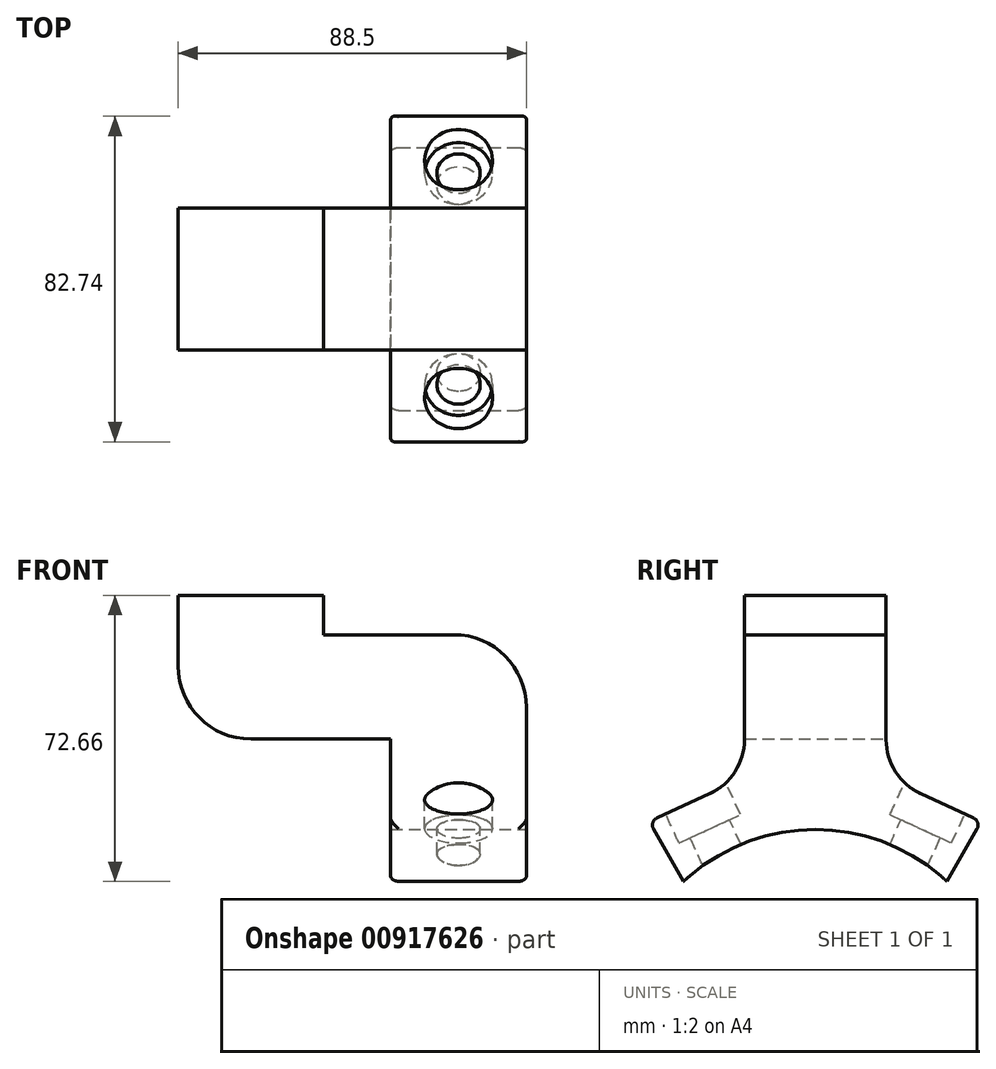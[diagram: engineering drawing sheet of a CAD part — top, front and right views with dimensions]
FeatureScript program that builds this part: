
annotation { "Feature Type Name" : "Feature", "Feature Type Description" : "" }
export const myFeature = defineFeature(function(context is Context, id is Id, definition is map)
    precondition{}
    {
        {
            var Q0;
            Q0=qCreatedBy(makeId("Front.planeOp"),FACE);
            var sketch = newSketch(context, id + "F0", { "sketchPlane" : qUnion([Q0])});
            skLineSegment(sketch, "E0", {"start": v(0, 0) * mm, "end": v(-88.5, 0) * mm});
            skLineSegment(sketch, "E1", {"start": v(-88.5, 0) * mm, "end": v(-88.5, 36.5) * mm});
            skLineSegment(sketch, "E2", {"start": v(-88.5, 36.5) * mm, "end": v(-51.5, 36.5) * mm});
            skLineSegment(sketch, "E3", {"start": v(-51.5, 36.5) * mm, "end": v(-51.5, 26.5) * mm});
            skLineSegment(sketch, "E4", {"start": v(-51.5, 26.5) * mm, "end": v(0, 26.5) * mm});
            skLineSegment(sketch, "E5", {"start": v(0, 26.5) * mm, "end": v(0, 0) * mm});
            skSolve(sketch);
        }
        {
            var Q0;
            Q0 = qSketchRegion(id + "F0", true);
            extrude(context, id + "F1", {"entities" : qUnion([Q0]), "endBound" : BoundingType.SYMMETRIC, "depth" : 36 * mm, "offsetDistance" : 25 * mm});
        }
        {
            var Q0;
            Q0=makeQuery(id+"F1.opExtrude","SWEPT_EDGE",EDGE,{"disambiguationData":[OSD([sQuery(id+"F0.wireOp",EDGE,"E4"),sQuery(id+"F0.wireOp",EDGE,"E5")])]});
            var Q1;
            Q1=makeQuery(id+"F1.opExtrude","SWEPT_EDGE",EDGE,{"disambiguationData":[OSD([sQuery(id+"F0.wireOp",EDGE,"E0"),sQuery(id+"F0.wireOp",EDGE,"E1")])]});
            fillet(context, id + "F2", {"entities" : qUnion([Q0, Q1]), "radius" : 18.5 * mm, "tangentPropagation" : true, "allowEdgeOverflow" : false});
        }
        {
            var Q0;
            Q0=makeQuery(id+"F1.opExtrude","SWEPT_FACE",FACE,{"disambiguationData":[OSD([sQuery(id+"F0.wireOp",EDGE,"E5")])]});
            var sketch = newSketch(context, id + "F3", { "sketchPlane" : qUnion([Q0])});
            skArc(sketch, "E6", {"start": v(-33.42, -36.16) * mm, "mid": v(0, -23) * mm, "end": v(33.42, -36.16) * mm});
            skArc(sketch, "E7", {"start": v(-41.07, -22.91) * mm, "mid": v(0, -8) * mm, "end": v(41.07, -22.91) * mm});
            skLineSegment(sketch, "E8", {"start": v(-41.07, -22.91) * mm, "end": v(-33.42, -36.16) * mm});
            skLineSegment(sketch, "E9", {"start": v(33.42, -36.16) * mm, "end": v(41.07, -22.91) * mm});
            skLineSegment(sketch, "E10", {"start": v(-33.42, -36.16) * mm, "end": v(0, -72) * mm, "construction": true});
            skLineSegment(sketch, "E11", {"start": v(0, -72) * mm, "end": v(33.42, -36.16) * mm, "construction": true});
            skLineSegment(sketch, "E12", {"start": v(-18, -10.58) * mm, "end": v(-18, 0) * mm});
            skLineSegment(sketch, "E13", {"start": v(-18, 0) * mm, "end": v(18, 0) * mm});
            skLineSegment(sketch, "E14", {"start": v(18, 0) * mm, "end": v(18, -10.58) * mm});
            skSolve(sketch);
        }
        {
            var Q0;
            Q0 = qSketchRegion(id + "F3", true);
            extrude(context, id + "F4", {"entities" : qUnion([Q0]), "operationType" : NewBodyOperationType.ADD, "oppositeDirection" : true, "depth" : 34.5 * mm, "offsetDistance" : 25 * mm});
        }
        {
            var Q0;
            Q0=makeQuery(id+"F4.opExtrude","SWEPT_EDGE",EDGE,{"disambiguationData":[OSD([sQuery(id+"F3.wireOp",EDGE,"E7"),sQuery(id+"F3.wireOp",EDGE,"E12")])]});
            var Q1;
            Q1=makeQuery(id+"F4.opExtrude","SWEPT_EDGE",EDGE,{"disambiguationData":[OSD([sQuery(id+"F3.wireOp",EDGE,"E7"),sQuery(id+"F3.wireOp",EDGE,"E14")])]});
            fillet(context, id + "F5", {"entities" : qUnion([Q0, Q1]), "radius" : 15 * mm, "tangentPropagation" : true, "allowEdgeOverflow" : false});
        }
        {
            var Q0;
            Q0=makeQuery(id+"F4.boolean.opBoolean","MERGE",FACE,{"derivedFrom":[makeQuery(id+"F1.opExtrude","SWEPT_FACE",FACE,{"disambiguationData":[OSD([sQuery(id+"F0.wireOp",EDGE,"E5")])]}),makeQuery(id+"F4.opExtrude","CAP_FACE",FACE,{"disambiguationData":[OSD([sQuery(id+"F3.wireOp",EDGE,"E6"),sQuery(id+"F3.wireOp",EDGE,"E7"),sQuery(id+"F3.wireOp",EDGE,"E8"),sQuery(id+"F3.wireOp",EDGE,"E9"),sQuery(id+"F3.wireOp",EDGE,"E12"),sQuery(id+"F3.wireOp",EDGE,"E13"),sQuery(id+"F3.wireOp",EDGE,"E14")])],"isStart":true})]});
            var sketch = newSketch(context, id + "F6", { "sketchPlane" : qUnion([Q0])});
            skLineSegment(sketch, "E15", {"start": v(-26.73, -13.85) * mm, "end": v(-42.2, -20.96) * mm});
            skLineSegment(sketch, "E16", {"start": v(-42.2, -20.96) * mm, "end": v(-41.07, -22.91) * mm});
            skLineSegment(sketch, "E17", {"start": v(-41.07, -22.91) * mm, "end": v(-26.73, -13.85) * mm});
            skLineSegment(sketch, "E18", {"start": v(26.73, -13.85) * mm, "end": v(42.2, -20.96) * mm});
            skLineSegment(sketch, "E19", {"start": v(42.2, -20.96) * mm, "end": v(41.07, -22.91) * mm});
            skLineSegment(sketch, "E20", {"start": v(41.07, -22.91) * mm, "end": v(26.73, -13.85) * mm});
            skSolve(sketch);
        }
        {
            var Q0;
            Q0 = qSketchRegion(id + "F6", true);
            extrude(context, id + "F7", {"entities" : qUnion([Q0]), "operationType" : NewBodyOperationType.ADD, "oppositeDirection" : true, "depth" : 34.5 * mm, "offsetDistance" : 25 * mm});
        }
        {
            var Q0;
            Q0=makeQuery(id+"F7.boolean.opBoolean","MERGE",FACE,{"derivedFrom":[makeQuery(id+"F4.boolean.opBoolean","MERGE",FACE,{"derivedFrom":[makeQuery(id+"F1.opExtrude","SWEPT_FACE",FACE,{"disambiguationData":[OSD([sQuery(id+"F0.wireOp",EDGE,"E5")])]}),makeQuery(id+"F4.opExtrude","CAP_FACE",FACE,{"disambiguationData":[OSD([sQuery(id+"F3.wireOp",EDGE,"E6"),sQuery(id+"F3.wireOp",EDGE,"E7"),sQuery(id+"F3.wireOp",EDGE,"E8"),sQuery(id+"F3.wireOp",EDGE,"E9"),sQuery(id+"F3.wireOp",EDGE,"E12"),sQuery(id+"F3.wireOp",EDGE,"E13"),sQuery(id+"F3.wireOp",EDGE,"E14")])],"isStart":true})]}),makeQuery(id+"F7.opExtrude","CAP_FACE",FACE,{"disambiguationData":[OSD([sQuery(id+"F6.wireOp",EDGE,"E15"),sQuery(id+"F6.wireOp",EDGE,"E16"),sQuery(id+"F6.wireOp",EDGE,"E17")])],"isStart":true}),makeQuery(id+"F7.opExtrude","CAP_FACE",FACE,{"disambiguationData":[OSD([sQuery(id+"F6.wireOp",EDGE,"E18"),sQuery(id+"F6.wireOp",EDGE,"E19"),sQuery(id+"F6.wireOp",EDGE,"E20")])],"isStart":true})]});
            var sketch = newSketch(context, id + "F8", { "sketchPlane" : qUnion([Q0])});
            skLineSegment(sketch, "E21", {"start": v(0, -72) * mm, "end": v(-30.99, -13.73) * mm});
            skLineSegment(sketch, "E22", {"start": v(0, -72) * mm, "end": v(30.99, -13.73) * mm});
            skSolve(sketch);
        }
        {
            var Q0;
            Q0=sQuery(id+"F8.wireOp",VERTEX,"E21.end");
            var Q1;
            Q1=makeQuery(id+"F7.opExtrude","SWEPT_FACE",FACE,{"disambiguationData":[OSD([sQuery(id+"F6.wireOp",EDGE,"E15")])]});
            cPlane(context, id + "F9", {"entities" : qUnion([Q0, Q1]), "cplaneType" : CPlaneType.PLANE_POINT, "offset" : 25 * mm, "width" : 150 * mm, "height" : 150 * mm});
        }
        {
            var Q0;
            Q0=qCreatedBy(id+"F9.planeOp",FACE);
            var sketch = newSketch(context, id + "F10", { "sketchPlane" : qUnion([Q0])});
            skLineSegment(sketch, "E23", {"start": v(0, -33.89) * mm, "end": v(-34.5, -33.89) * mm});
            skPoint(sketch, "E24", {"position": v(-17.25, -33.89) * mm});
            skSolve(sketch);
        }
        {
            var Q0;
            Q0=sQuery(id+"F10.wireOp",VERTEX,"E24");
            var Q1;
            Q1=makeQuery(id+"F1.opExtrude","SWEPT_BODY",BODY,{"disambiguationData":[OSD([sQuery(id+"F0.wireOp",EDGE,"E0"),sQuery(id+"F0.wireOp",EDGE,"E1"),sQuery(id+"F0.wireOp",EDGE,"E2"),sQuery(id+"F0.wireOp",EDGE,"E3"),sQuery(id+"F0.wireOp",EDGE,"E4"),sQuery(id+"F0.wireOp",EDGE,"E5")])]});
            hole(context, id + "F11", {"style" : HoleStyle.C_BORE, "endStyle" : HoleEndStyle.THROUGH, "standardTappedOrClearance" : lookupTablePath({ "fit" : "Normal", "standard" : "ISO", "size" : "M10", "type" : "Clearance" }), "standardBlindInLast" : lookupTablePath({ "fit" : "Normal", "standard" : "ISO", "size" : "M10", "type" : "Clearance" }), "holeDiameter" : 11 * mm, "cBoreDiameter" : 17.25 * mm, "cBoreDepth" : 10 * mm, "majorDiameter" : 5 * mm, "isTappedThrough" : true, "tappedDepth" : 12 * mm, "tapClearance" : 3, "startFromSketch" : true, "locations" : qUnion([Q0]), "scope" : qUnion([Q1])});
        }
        {
            var Q0;
            Q0=sQuery(id+"F8.wireOp",VERTEX,"E22.end");
            var Q1;
            Q1=makeQuery(id+"F7.opExtrude","SWEPT_FACE",FACE,{"disambiguationData":[OSD([sQuery(id+"F6.wireOp",EDGE,"E18")])]});
            cPlane(context, id + "F12", {"entities" : qUnion([Q0, Q1]), "cplaneType" : CPlaneType.PLANE_POINT, "offset" : 25 * mm, "width" : 150 * mm, "height" : 150 * mm});
        }
        {
            var Q0;
            Q0=qCreatedBy(id+"F12.planeOp",FACE);
            var sketch = newSketch(context, id + "F13", { "sketchPlane" : qUnion([Q0])});
            skLineSegment(sketch, "E25", {"start": v(0, 33.89) * mm, "end": v(-34.5, 33.89) * mm});
            skPoint(sketch, "E26", {"position": v(-17.25, 33.89) * mm});
            skSolve(sketch);
        }
        {
            var Q0;
            Q0=sQuery(id+"F13.wireOp",VERTEX,"E26");
            var Q1;
            Q1=makeQuery(id+"F1.opExtrude","SWEPT_BODY",BODY,{"disambiguationData":[OSD([sQuery(id+"F0.wireOp",EDGE,"E0"),sQuery(id+"F0.wireOp",EDGE,"E1"),sQuery(id+"F0.wireOp",EDGE,"E2"),sQuery(id+"F0.wireOp",EDGE,"E3"),sQuery(id+"F0.wireOp",EDGE,"E4"),sQuery(id+"F0.wireOp",EDGE,"E5")])]});
            hole(context, id + "F14", {"style" : HoleStyle.C_BORE, "endStyle" : HoleEndStyle.THROUGH, "standardTappedOrClearance" : lookupTablePath({ "fit" : "Normal", "standard" : "ISO", "size" : "M10", "type" : "Clearance" }), "standardBlindInLast" : lookupTablePath({ "fit" : "Normal", "standard" : "ISO", "size" : "M10", "type" : "Clearance" }), "holeDiameter" : 11 * mm, "cBoreDiameter" : 17.25 * mm, "cBoreDepth" : 10 * mm, "majorDiameter" : 5 * mm, "isTappedThrough" : true, "tappedDepth" : 12 * mm, "tapClearance" : 3, "startFromSketch" : true, "locations" : qUnion([Q0]), "scope" : qUnion([Q1])});
        }
        {
            var Q0;
            Q0=makeQuery(id+"F7.boolean.opBoolean","MERGE",EDGE,{"derivedFrom":[makeQuery(id+"F4.opExtrude","CAP_EDGE",EDGE,{"disambiguationData":[OSD([sQuery(id+"F3.wireOp",EDGE,"E8")])],"isStart":true}),makeQuery(id+"F7.opExtrude","CAP_EDGE",EDGE,{"disambiguationData":[OSD([sQuery(id+"F6.wireOp",EDGE,"E16")])],"isStart":true})]});
            var Q1;
            Q1=makeQuery(id+"F7.opExtrude","SWEPT_EDGE",EDGE,{"disambiguationData":[OSD([sQuery(id+"F6.wireOp",EDGE,"E15"),sQuery(id+"F6.wireOp",EDGE,"E16")])]});
            var Q2;
            Q2=makeQuery(id+"F7.boolean.opBoolean","MERGE",EDGE,{"derivedFrom":[makeQuery(id+"F4.opExtrude","CAP_EDGE",EDGE,{"disambiguationData":[OSD([sQuery(id+"F3.wireOp",EDGE,"E8")])],"isStart":false}),makeQuery(id+"F7.opExtrude","CAP_EDGE",EDGE,{"disambiguationData":[OSD([sQuery(id+"F6.wireOp",EDGE,"E16")])],"isStart":false})]});
            var Q3;
            Q3=makeQuery(id+"F7.opExtrude","SWEPT_EDGE",EDGE,{"disambiguationData":[OSD([sQuery(id+"F6.wireOp",EDGE,"E18"),sQuery(id+"F6.wireOp",EDGE,"E19")])]});
            var Q4;
            Q4=makeQuery(id+"F7.boolean.opBoolean","MERGE",EDGE,{"derivedFrom":[makeQuery(id+"F4.opExtrude","CAP_EDGE",EDGE,{"disambiguationData":[OSD([sQuery(id+"F3.wireOp",EDGE,"E9")])],"isStart":true}),makeQuery(id+"F7.opExtrude","CAP_EDGE",EDGE,{"disambiguationData":[OSD([sQuery(id+"F6.wireOp",EDGE,"E19")])],"isStart":true})]});
            var Q5;
            Q5=makeQuery(id+"F7.boolean.opBoolean","MERGE",EDGE,{"derivedFrom":[makeQuery(id+"F4.opExtrude","CAP_EDGE",EDGE,{"disambiguationData":[OSD([sQuery(id+"F3.wireOp",EDGE,"E9")])],"isStart":false}),makeQuery(id+"F7.opExtrude","CAP_EDGE",EDGE,{"disambiguationData":[OSD([sQuery(id+"F6.wireOp",EDGE,"E19")])],"isStart":false})]});
            fillet(context, id + "F15", {"entities" : qUnion([Q0, Q1, Q2, Q3, Q4, Q5]), "radius" : 2 * mm, "tangentPropagation" : true, "allowEdgeOverflow" : false});
        }
    });
